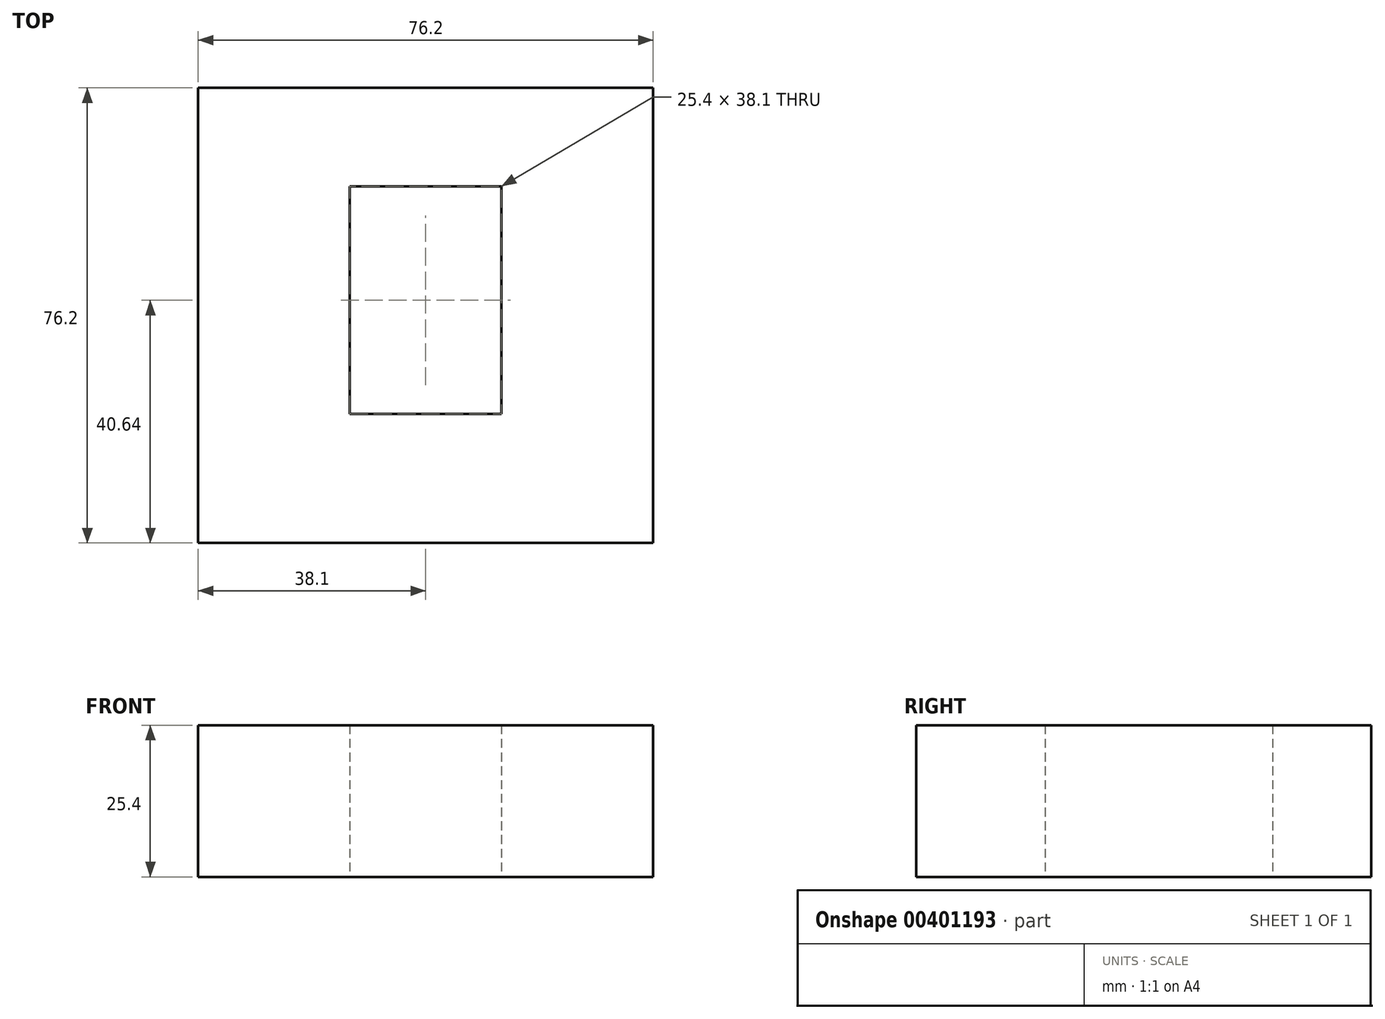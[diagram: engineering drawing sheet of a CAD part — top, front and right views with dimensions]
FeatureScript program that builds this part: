
annotation { "Feature Type Name" : "Feature", "Feature Type Description" : "" }
export const myFeature = defineFeature(function(context is Context, id is Id, definition is map)
    precondition{}
    {
        {
            var Q0;
            Q0=qCreatedBy(makeId("Top.planeOp"),FACE);
            var sketch = newSketch(context, id + "F0", { "sketchPlane" : qUnion([Q0])});
            skLineSegment(sketch, "E0.bottom", {"start": v(0, 0) * mm, "end": v(25.4, 0) * mm});
            skLineSegment(sketch, "E0.top", {"start": v(0, 38.1) * mm, "end": v(25.4, 38.1) * mm});
            skLineSegment(sketch, "E0.left", {"start": v(0, 0) * mm, "end": v(0, 38.1) * mm});
            skLineSegment(sketch, "E0.right", {"start": v(25.4, 0) * mm, "end": v(25.4, 38.1) * mm});
            skLineSegment(sketch, "E1.bottom", {"start": v(-25.4, 54.61) * mm, "end": v(50.8, 54.61) * mm});
            skLineSegment(sketch, "E1.top", {"start": v(-25.4, -21.59) * mm, "end": v(50.8, -21.59) * mm});
            skLineSegment(sketch, "E1.left", {"start": v(-25.4, 54.61) * mm, "end": v(-25.4, -21.59) * mm});
            skLineSegment(sketch, "E1.right", {"start": v(50.8, 54.61) * mm, "end": v(50.8, -21.59) * mm});
            skSolve(sketch);
        }
        {
            var Q0;
            Q0=makeQuery(id+"F0.imprint","IMPRINT",FACE,{"disambiguationData":[TD([[makeQuery(id+"F0.imprint","IMPRINT",EDGE,{"derivedFrom":sQuery(id+"F0.wireOp",EDGE,"E0.bottom")}),-1.0]])]});
            extrude(context, id + "F1", {"entities" : qUnion([Q0]), "depth" : 25.4 * mm});
        }
    });
